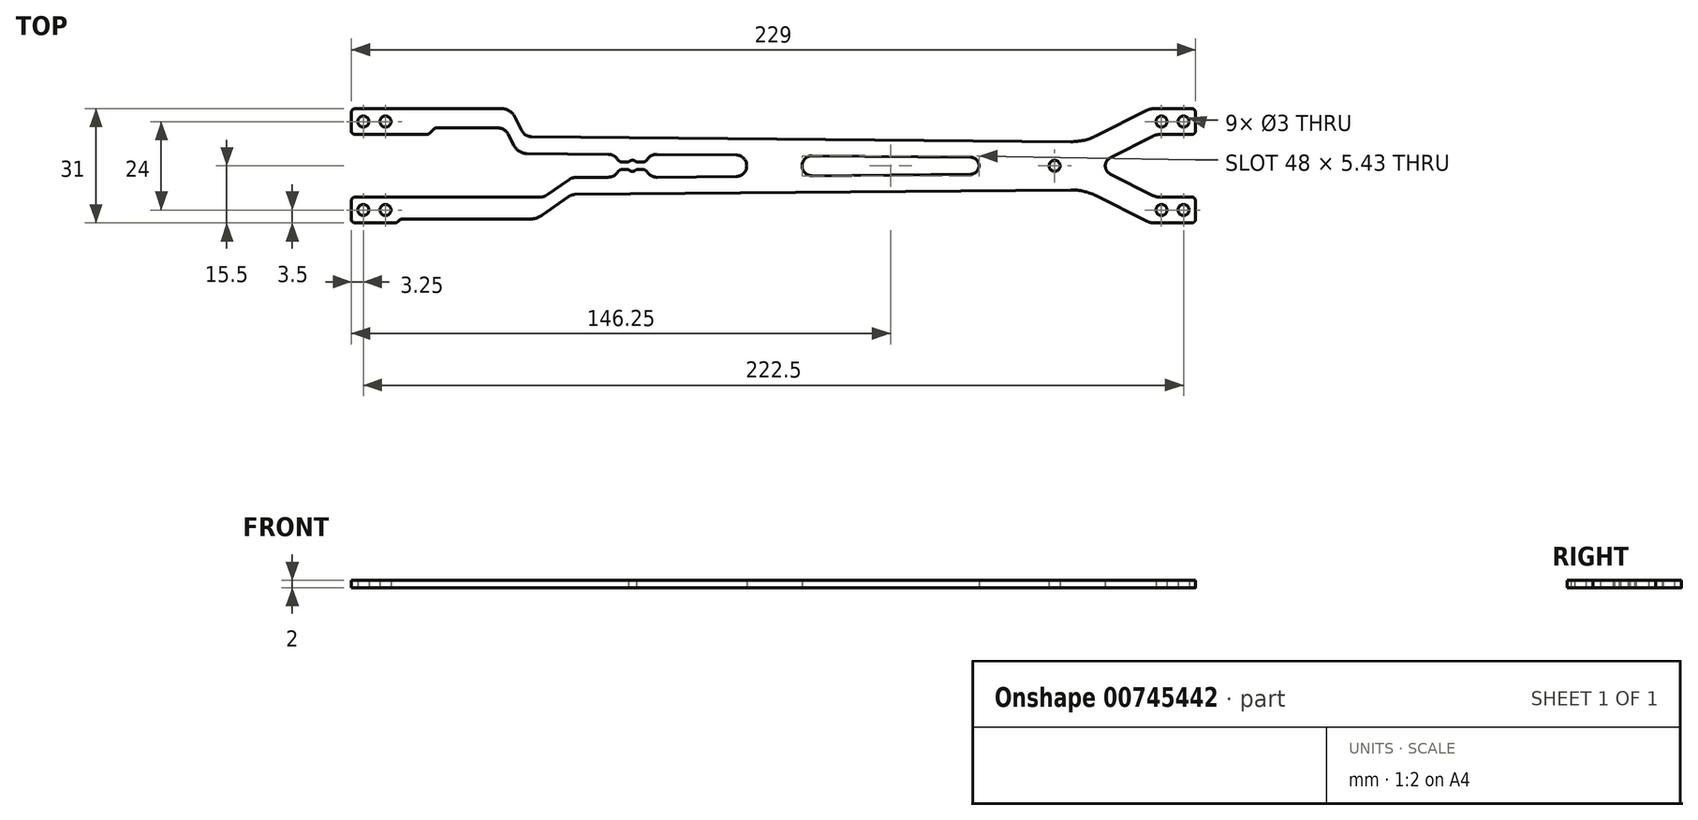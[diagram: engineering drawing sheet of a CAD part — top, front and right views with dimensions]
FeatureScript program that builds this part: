
annotation { "Feature Type Name" : "Feature", "Feature Type Description" : "" }
export const myFeature = defineFeature(function(context is Context, id is Id, definition is map)
    precondition{}
    {
        {
            var Q0;
            Q0=qCreatedBy(makeId("Top.planeOp"),FACE);
            var sketch = newSketch(context, id + "F0", { "sketchPlane" : qUnion([Q0])});
            skCircle(sketch, "E0", {"center": v(-91.08, -12) * mm, "radius": 1.5 * mm});
            skCircle(sketch, "E1", {"center": v(131.42, -12) * mm, "radius": 1.5 * mm});
            skCircle(sketch, "E2", {"center": v(-85.08, -12) * mm, "radius": 1.5 * mm});
            skCircle(sketch, "E3", {"center": v(-91.08, 12) * mm, "radius": 1.5 * mm});
            skCircle(sketch, "E4", {"center": v(-85.08, 12) * mm, "radius": 1.5 * mm});
            skCircle(sketch, "E5", {"center": v(131.42, 12) * mm, "radius": 1.5 * mm});
            skCircle(sketch, "E6", {"center": v(125.42, 12) * mm, "radius": 1.5 * mm});
            skCircle(sketch, "E7", {"center": v(125.42, -12) * mm, "radius": 1.5 * mm});
            skCircle(sketch, "E8", {"center": v(96.42, 0) * mm, "radius": 1.5 * mm});
            skArc(sketch, "E9", {"start": v(-16.96, 1) * mm, "mid": v(-18.08, 1.5) * mm, "end": v(-19.2, 1) * mm});
            skLineSegment(sketch, "E10", {"start": v(-94.33, -14.5) * mm, "end": v(-94.33, -9.5) * mm});
            skLineSegment(sketch, "E11", {"start": v(-93.33, -8.5) * mm, "end": v(-43.09, -8.5) * mm});
            skLineSegment(sketch, "E12", {"start": v(123.5, -15.5) * mm, "end": v(133.67, -15.5) * mm});
            skLineSegment(sketch, "E13", {"start": v(134.67, -14.5) * mm, "end": v(134.67, -9.5) * mm});
            skLineSegment(sketch, "E14", {"start": v(133.67, -8.5) * mm, "end": v(124.92, -8.5) * mm});
            skLineSegment(sketch, "E15", {"start": v(123.12, -8.07) * mm, "end": v(111.54, -2.23) * mm});
            skLineSegment(sketch, "E16.0", {"start": v(121.24, -14.96) * mm, "end": v(107.73, -8.15) * mm});
            skLineSegment(sketch, "E17", {"start": v(100.84, -6.54) * mm, "end": v(-33.67, -7.79) * mm});
            skLineSegment(sketch, "E18", {"start": v(-42.62, -13.41) * mm, "end": v(-35.36, -8.33) * mm});
            skLineSegment(sketch, "E19", {"start": v(-33.64, -3.19) * mm, "end": v(-24.65, -3.1) * mm});
            skLineSegment(sketch, "E20", {"start": v(-41.37, -7.96) * mm, "end": v(-35.33, -3.73) * mm});
            skLineSegment(sketch, "E21.MirrorCS", {"start": v(123.12, 8.07) * mm, "end": v(111.54, 2.23) * mm});
            skLineSegment(sketch, "E22.MirrorCS", {"start": v(133.67, 8.5) * mm, "end": v(124.92, 8.5) * mm});
            skLineSegment(sketch, "E23.MirrorCS", {"start": v(-93.33, 15.5) * mm, "end": v(-53.58, 15.5) * mm});
            skLineSegment(sketch, "E24.MirrorCS", {"start": v(134.67, 14.5) * mm, "end": v(134.67, 9.5) * mm});
            skLineSegment(sketch, "E25.MirrorCS", {"start": v(121.24, 14.96) * mm, "end": v(107.73, 8.15) * mm});
            skLineSegment(sketch, "E26.MirrorCS", {"start": v(123.5, 15.5) * mm, "end": v(133.67, 15.5) * mm});
            skLineSegment(sketch, "E27.MirrorCS", {"start": v(100.84, 6.54) * mm, "end": v(-45.44, 7.9) * mm});
            skLineSegment(sketch, "E28", {"start": v(-48.08, 9.53) * mm, "end": v(-50.02, 13.32) * mm});
            skLineSegment(sketch, "E29", {"start": v(-94.33, 14.5) * mm, "end": v(-94.33, 9.5) * mm});
            skLineSegment(sketch, "E30", {"start": v(-11.45, -3.1) * mm, "end": v(10.04, -2.9) * mm});
            skLineSegment(sketch, "E31.MirrorCS", {"start": v(-11.45, 3.1) * mm, "end": v(10.04, 2.9) * mm});
            skArc(sketch, "E32", {"start": v(-11.45, 3.1) * mm, "mid": v(-12.95, 2.73) * mm, "end": v(-14.08, 1.69) * mm});
            skArc(sketch, "E33", {"start": v(73.63, -2.32) * mm, "mid": v(75.92, 0) * mm, "end": v(73.63, 2.32) * mm});
            skLineSegment(sketch, "E34.trimOffspring", {"start": v(30.66, -2.71) * mm, "end": v(73.63, -2.32) * mm});
            skLineSegment(sketch, "E35.trimOffspring", {"start": v(30.66, 2.71) * mm, "end": v(73.63, 2.32) * mm});
            skArc(sketch, "E36", {"start": v(10.04, -2.9) * mm, "mid": v(12.92, 0) * mm, "end": v(10.04, 2.9) * mm});
            skArc(sketch, "E37", {"start": v(30.66, 2.71) * mm, "mid": v(27.92, 0) * mm, "end": v(30.66, -2.71) * mm});
            skLineSegment(sketch, "E38", {"start": v(-35.33, -3.73) * mm, "end": v(-41.37, -7.96) * mm});
            skLineSegment(sketch, "E39.MirrorCS", {"start": v(-71.33, 10.25) * mm, "end": v(-54.5, 10.25) * mm});
            skLineSegment(sketch, "E40.MirrorCS", {"start": v(-72.04, 9.96) * mm, "end": v(-73.2, 8.8) * mm});
            skLineSegment(sketch, "E41.MirrorCS", {"start": v(-93.33, 8.5) * mm, "end": v(-73.9, 8.5) * mm});
            skArc(sketch, "E42.filletArc", {"start": v(-71.33, 10.25) * mm, "mid": v(-71.71, 10.17) * mm, "end": v(-72.04, 9.96) * mm});
            skArc(sketch, "E43.filletArc", {"start": v(-73.9, 8.5) * mm, "mid": v(-73.53, 8.58) * mm, "end": v(-73.2, 8.8) * mm});
            skArc(sketch, "E44.filletArc", {"start": v(-33.64, -3.19) * mm, "mid": v(-34.52, -3.33) * mm, "end": v(-35.33, -3.73) * mm});
            skArc(sketch, "E45.filletArc", {"start": v(-48.08, 9.53) * mm, "mid": v(-46.99, 8.34) * mm, "end": v(-45.44, 7.9) * mm});
            skArc(sketch, "E46.filletArc", {"start": v(-33.67, -7.79) * mm, "mid": v(-34.56, -7.93) * mm, "end": v(-35.36, -8.33) * mm});
            skArc(sketch, "E47.filletArc", {"start": v(-50.02, 13.32) * mm, "mid": v(-51.5, 14.91) * mm, "end": v(-53.58, 15.5) * mm});
            skArc(sketch, "E48.filletArc", {"start": v(-94.33, -14.5) * mm, "mid": v(-94.04, -15.2) * mm, "end": v(-93.33, -15.5) * mm});
            skArc(sketch, "E49.filletArc", {"start": v(-93.33, -8.5) * mm, "mid": v(-94.04, -8.8) * mm, "end": v(-94.33, -9.5) * mm});
            skArc(sketch, "E50.filletArc", {"start": v(-94.33, 9.5) * mm, "mid": v(-94.04, 8.8) * mm, "end": v(-93.33, 8.5) * mm});
            skArc(sketch, "E51.filletArc", {"start": v(-93.33, 15.5) * mm, "mid": v(-94.04, 15.2) * mm, "end": v(-94.33, 14.5) * mm});
            skArc(sketch, "E52.filletArc", {"start": v(134.67, 14.5) * mm, "mid": v(134.38, 15.2) * mm, "end": v(133.67, 15.5) * mm});
            skArc(sketch, "E53.filletArc", {"start": v(133.67, 8.5) * mm, "mid": v(134.38, 8.8) * mm, "end": v(134.67, 9.5) * mm});
            skArc(sketch, "E54.filletArc", {"start": v(134.67, -9.5) * mm, "mid": v(134.38, -8.8) * mm, "end": v(133.67, -8.5) * mm});
            skArc(sketch, "E55.filletArc", {"start": v(133.67, -15.5) * mm, "mid": v(134.38, -15.2) * mm, "end": v(134.67, -14.5) * mm});
            skArc(sketch, "E56.filletArc", {"start": v(124.92, 8.5) * mm, "mid": v(124, 8.4) * mm, "end": v(123.12, 8.07) * mm});
            skArc(sketch, "E57.filletArc", {"start": v(123.12, -8.07) * mm, "mid": v(124, -8.4) * mm, "end": v(124.92, -8.5) * mm});
            skArc(sketch, "E58.filletArc", {"start": v(123.5, 15.5) * mm, "mid": v(122.34, 15.36) * mm, "end": v(121.24, 14.96) * mm});
            skArc(sketch, "E59.filletArc", {"start": v(121.24, -14.96) * mm, "mid": v(122.34, -15.36) * mm, "end": v(123.5, -15.5) * mm});
            skPoint(sketch, "E60.visualSharp", {"position": v(105.24, -6.5) * mm});
            skArc(sketch, "E60.filletArc", {"start": v(107.73, -8.15) * mm, "mid": v(104.38, -6.93) * mm, "end": v(100.84, -6.54) * mm});
            skPoint(sketch, "E61.visualSharp", {"position": v(105.27, 6.52) * mm});
            skArc(sketch, "E61.filletArc", {"start": v(100.84, 6.54) * mm, "mid": v(104.38, 6.93) * mm, "end": v(107.73, 8.15) * mm});
            skArc(sketch, "E62.filletArc", {"start": v(111.54, 2.23) * mm, "mid": v(110.17, 0) * mm, "end": v(111.54, -2.23) * mm});
            skLineSegment(sketch, "E63.MirrorCS", {"start": v(-46.7, 3.3) * mm, "end": v(-24.65, 3.1) * mm});
            skLineSegment(sketch, "E64", {"start": v(-50.22, 5.49) * mm, "end": v(-51.82, 8.62) * mm});
            skArc(sketch, "E65.filletArc", {"start": v(-43.09, -8.5) * mm, "mid": v(-42.19, -8.36) * mm, "end": v(-41.37, -7.96) * mm});
            skLineSegment(sketch, "E66", {"start": v(-93.33, -15.5) * mm, "end": v(-82.5, -15.5) * mm});
            skLineSegment(sketch, "E67", {"start": v(-81.58, -14.59) * mm, "end": v(-81.58, -14.59) * mm});
            skLineSegment(sketch, "E68", {"start": v(-80.67, -14.5) * mm, "end": v(-46.07, -14.5) * mm});
            skPoint(sketch, "E69.visualSharp", {"position": v(-44.17, -14.5) * mm});
            skArc(sketch, "E69.filletArc", {"start": v(-46.07, -14.5) * mm, "mid": v(-44.26, -14.22) * mm, "end": v(-42.62, -13.41) * mm});
            skPoint(sketch, "E70.visualSharp", {"position": v(-81.58, -14.5) * mm});
            skPoint(sketch, "E71.visualSharp", {"position": v(-81.58, -15.5) * mm});
            skArc(sketch, "E72", {"start": v(-24.65, 3.1) * mm, "mid": v(-23.19, 2.72) * mm, "end": v(-22.08, 1.69) * mm});
            skPoint(sketch, "E73.visualSharp", {"position": v(-48.66, 2.43) * mm});
            skArc(sketch, "E73.filletArc", {"start": v(-50.22, 5.49) * mm, "mid": v(-48.77, 3.9) * mm, "end": v(-46.7, 3.3) * mm});
            skLineSegment(sketch, "E74", {"start": v(-81.79, -15.2) * mm, "end": v(-81.37, -14.8) * mm});
            skPoint(sketch, "E75.visualSharp", {"position": v(-81.08, -14.5) * mm});
            skArc(sketch, "E75.filletArc", {"start": v(-80.67, -14.5) * mm, "mid": v(-81.05, -14.58) * mm, "end": v(-81.37, -14.8) * mm});
            skPoint(sketch, "E76.visualSharp", {"position": v(-82.08, -15.5) * mm});
            skArc(sketch, "E76.filletArc", {"start": v(-82.5, -15.5) * mm, "mid": v(-82.11, -15.42) * mm, "end": v(-81.79, -15.2) * mm});
            skPoint(sketch, "E77.orphan", {"position": v(-50.86, 6.73) * mm});
            skPoint(sketch, "E78.visualSharp", {"position": v(-52.66, 10.25) * mm});
            skArc(sketch, "E78.filletArc", {"start": v(-51.82, 8.62) * mm, "mid": v(-52.93, 9.8) * mm, "end": v(-54.5, 10.25) * mm});
            skLineSegment(sketch, "E79", {"start": v(-20.82, -1) * mm, "end": v(-19.2, -1) * mm});
            skLineSegment(sketch, "E80.MirrorCS", {"start": v(-20.82, 1) * mm, "end": v(-19.2, 1) * mm});
            skArc(sketch, "E81.trimOffspring", {"start": v(-14.08, -1.69) * mm, "mid": v(-12.95, -2.73) * mm, "end": v(-11.45, -3.1) * mm});
            skLineSegment(sketch, "E82.trimOffspring", {"start": v(-16.96, 1) * mm, "end": v(-15.34, 1) * mm});
            skLineSegment(sketch, "E83.trimOffspring", {"start": v(-16.96, -1) * mm, "end": v(-15.34, -1) * mm});
            skArc(sketch, "E84.trimOffspring", {"start": v(-19.2, -1) * mm, "mid": v(-18.08, -1.5) * mm, "end": v(-16.96, -1) * mm});
            skArc(sketch, "E85.trimOffspring", {"start": v(-22.08, -1.69) * mm, "mid": v(-23.19, -2.72) * mm, "end": v(-24.65, -3.1) * mm});
            skPoint(sketch, "E86.visualSharp", {"position": v(-21.75, 1) * mm});
            skArc(sketch, "E86.filletArc", {"start": v(-22.08, 1.69) * mm, "mid": v(-21.53, 1.18) * mm, "end": v(-20.82, 1) * mm});
            skPoint(sketch, "E87.visualSharp", {"position": v(-21.75, -1) * mm});
            skArc(sketch, "E87.filletArc", {"start": v(-20.82, -1) * mm, "mid": v(-21.53, -1.18) * mm, "end": v(-22.08, -1.69) * mm});
            skPoint(sketch, "E88.visualSharp", {"position": v(-14.41, -1) * mm});
            skArc(sketch, "E88.filletArc", {"start": v(-14.08, -1.69) * mm, "mid": v(-14.62, -1.18) * mm, "end": v(-15.34, -1) * mm});
            skPoint(sketch, "E89.visualSharp", {"position": v(-14.41, 1) * mm});
            skArc(sketch, "E89.filletArc", {"start": v(-15.34, 1) * mm, "mid": v(-14.62, 1.18) * mm, "end": v(-14.08, 1.69) * mm});
            skSolve(sketch);
        }
        {
            var Q0;
            Q0=makeQuery(id+"F0.imprint","IMPRINT",FACE,{"disambiguationData":[TD([[makeQuery(id+"F0.imprint","IMPRINT",EDGE,{"derivedFrom":sQuery(id+"F0.wireOp",EDGE,"E0")}),-1.0]])]});
            extrude(context, id + "F1", {"entities" : qUnion([Q0]), "depth" : 2 * mm, "offsetDistance" : 25 * mm});
        }
    });
